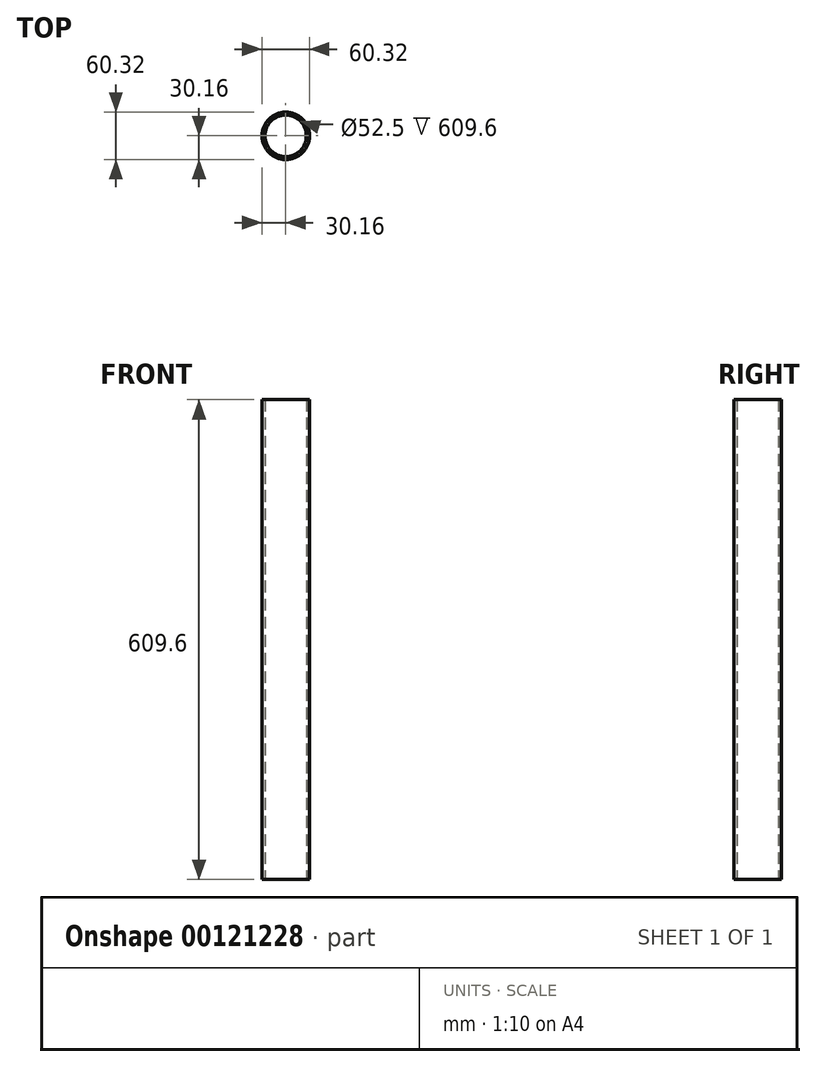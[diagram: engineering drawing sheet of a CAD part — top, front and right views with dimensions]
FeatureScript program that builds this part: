
annotation { "Feature Type Name" : "Feature", "Feature Type Description" : "" }
export const myFeature = defineFeature(function(context is Context, id is Id, definition is map)
    precondition{}
    {
        {
            var Q0;
            Q0=qCreatedBy(makeId("Top.planeOp"),FACE);
            var sketch = newSketch(context, id + "F0", { "sketchPlane" : qUnion([Q0])});
            skCircle(sketch, "E0", {"center": v(0, 0) * mm, "radius": 30.16 * mm});
            skCircle(sketch, "E1", {"center": v(0, 0) * mm, "radius": 26.25 * mm});
            skSolve(sketch);
        }
        {
            var Q0;
            Q0=makeQuery(id+"F0.imprint","IMPRINT",FACE,{"disambiguationData":[TD([[makeQuery(id+"F0.imprint","IMPRINT",EDGE,{"derivedFrom":sQuery(id+"F0.wireOp",EDGE,"E0")}),1.0]])]});
            extrude(context, id + "F1", {"entities" : qUnion([Q0]), "depth" : 609.6 * mm});
        }
    });
